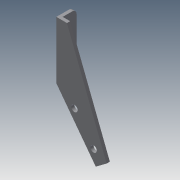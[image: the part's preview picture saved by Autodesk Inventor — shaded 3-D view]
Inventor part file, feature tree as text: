
AUTODESK INVENTOR PART (.ipt)
format: ipt  version: 2013 (Build 170138000, 138)  size: 152,576 bytes
history: native  units: mm
features: sketch x12, extrude x7, fillet x2
ambient origin geometry x8: Origin, YZ Plane, XZ Plane, XY Plane, X Axis, Y Axis, Z Axis, Center Point
bodies: Solid1 (feature_tree)
feature tree (21):
  sketch  "Sketch1"  dims[d4=3.0mm d5=3.0mm d6=2.0mm d7=0.0mm]
  extrude  "Extrusion1"  Depth=2.0mm TaperAngle=0.0deg
  extrude  "Extrusion2"  Depth=2.0mm TaperAngle=0.0deg
  extrude  "Extrusion3"  Depth=2.0mm TaperAngle=0.0deg
  sketch  "Sketch5"  dims[d21=10.0mm d22=0.0mm d23=0.5mm d24=0.0mm]
  extrude  "Extrusion4"  Depth=6.0mm TaperAngle=0.0deg
  sketch  "Sketch7"  dims[d28=2.0mm]
  sketch  "Sketch8"
  extrude  "Extrusion5"  Depth=0.5mm TaperAngle=0.0deg
  extrude  "Extrusion6"  Depth=2.0mm
  extrude  "Extrusion7"  [1 undecoded]
  fillet  "Fillet1"  [1 undecoded]
  fillet  "Fillet2"  [1 undecoded]
  sketch  "Sketch12"
  sketch  "Sketch2"  dims[d8=10.0mm d11=2.0mm d12=0.0mm]
  sketch  "Sketch3"  dims[d13=5.0mm d14=2.0mm d15=0.0mm]
  sketch  "Sketch4"  dims[d16=2.0mm d17=6.0mm d18=0.0mm]
  sketch  "Sketch6"  dims[d25=0.5mm d26=0.0mm d27=2.0mm]
  sketch  "Sketch9"
  sketch  "Sketch10"
  sketch  "Sketch11"
note: 3 required parameter values undecoded (feature->parameter linkage not recoverable at this tier; creation-order binding heuristic only, values carry confidence <= 0.55)
